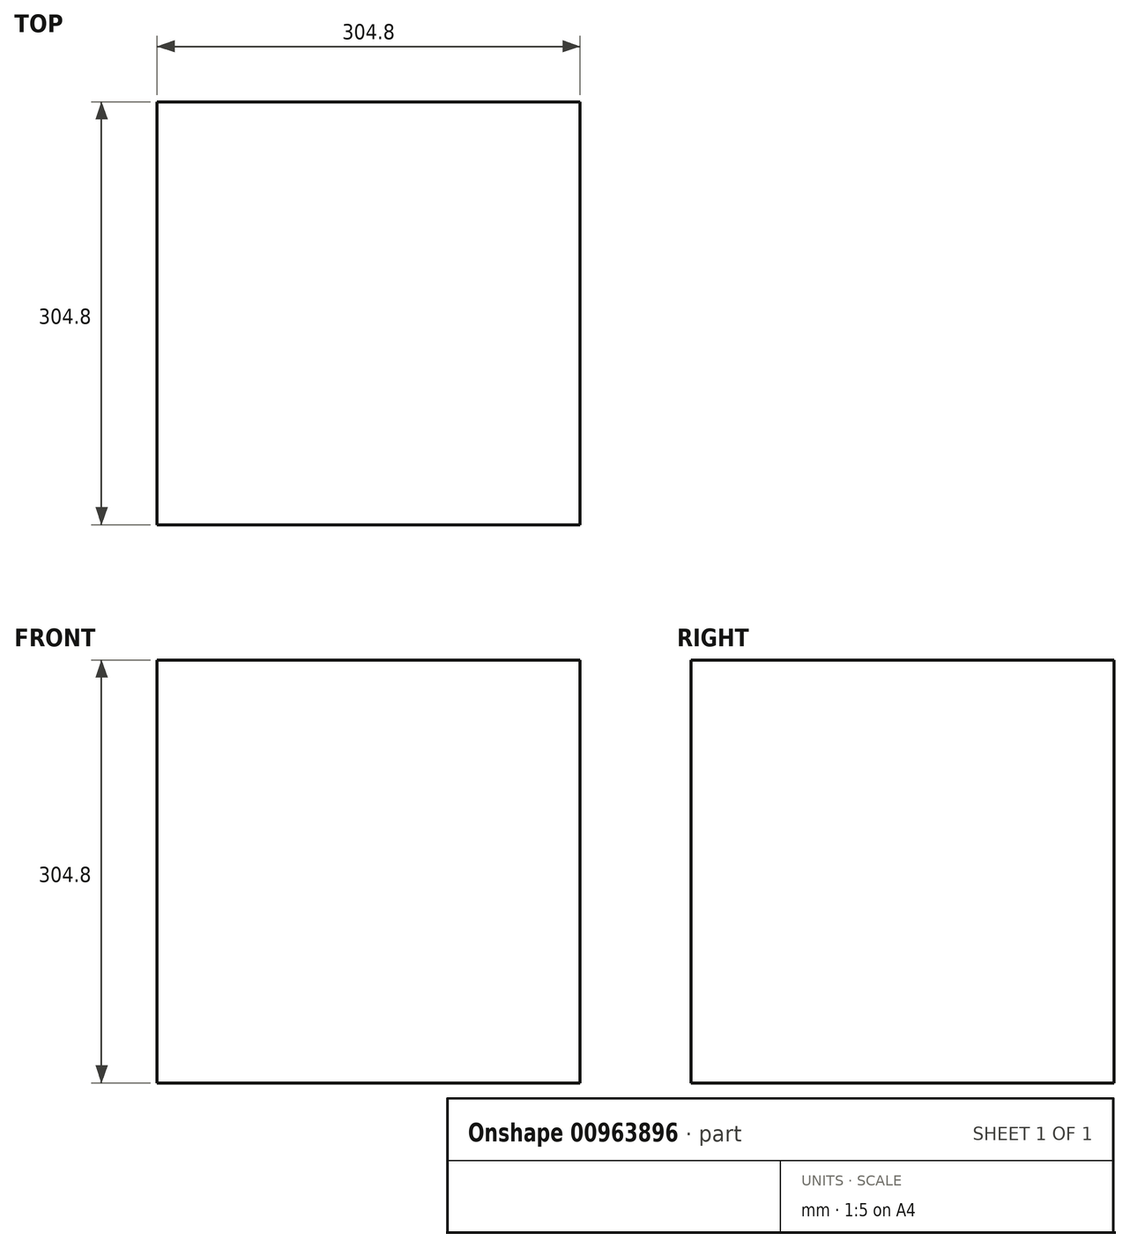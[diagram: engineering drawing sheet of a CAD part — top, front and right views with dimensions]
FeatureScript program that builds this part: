
annotation { "Feature Type Name" : "Feature", "Feature Type Description" : "" }
export const myFeature = defineFeature(function(context is Context, id is Id, definition is map)
    precondition{}
    {
        {
            var Q0;
            Q0=qCreatedBy(makeId("Top.planeOp"),FACE);
            var sketch = newSketch(context, id + "F0", { "sketchPlane" : qUnion([Q0])});
            skLineSegment(sketch, "E0.bottom", {"start": v(152.4, 152.4) * mm, "end": v(-152.4, 152.4) * mm});
            skLineSegment(sketch, "E0.top", {"start": v(152.4, -152.4) * mm, "end": v(-152.4, -152.4) * mm});
            skLineSegment(sketch, "E0.left", {"start": v(152.4, 152.4) * mm, "end": v(152.4, -152.4) * mm});
            skLineSegment(sketch, "E0.right", {"start": v(-152.4, 152.4) * mm, "end": v(-152.4, -152.4) * mm});
            skPoint(sketch, "E0.middle", {"position": v(0, 0) * mm});
            skSolve(sketch);
        }
        {
            var Q0;
            Q0=makeQuery(id+"F0.imprint","IMPRINT",FACE,{"disambiguationData":[TD([[makeQuery(id+"F0.imprint","IMPRINT",EDGE,{"derivedFrom":sQuery(id+"F0.wireOp",EDGE,"E0.bottom")}),1.0]])]});
            extrude(context, id + "F1", {"entities" : qUnion([Q0]), "depth" : 304.8 * mm, "offsetDistance" : 25.4 * mm});
        }
    });
